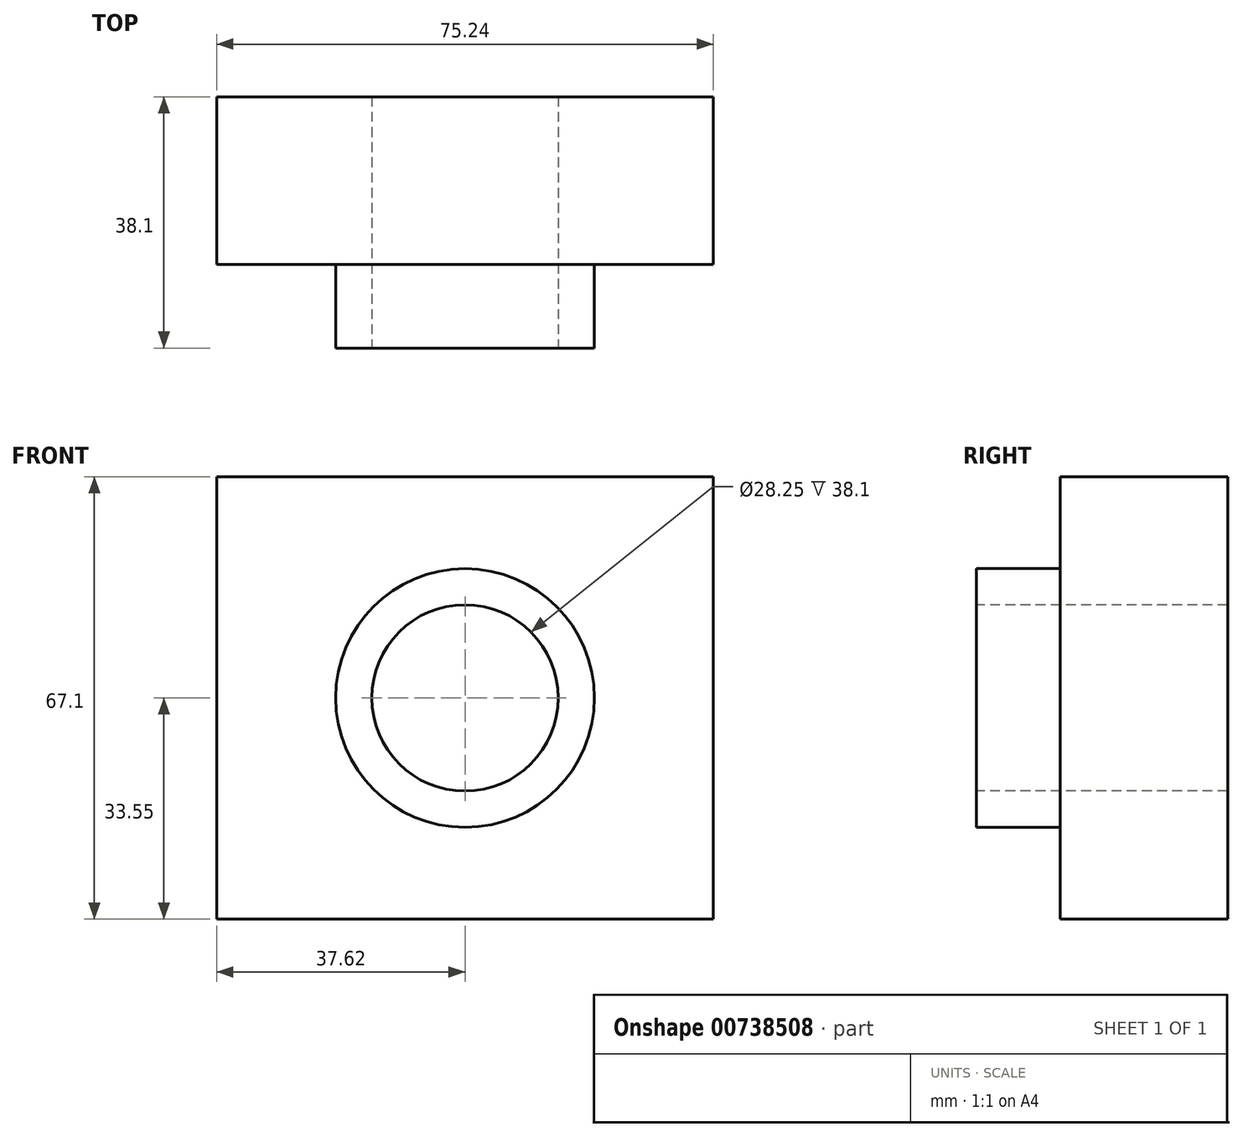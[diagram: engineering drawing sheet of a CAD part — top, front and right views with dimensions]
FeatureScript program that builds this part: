
annotation { "Feature Type Name" : "Feature", "Feature Type Description" : "" }
export const myFeature = defineFeature(function(context is Context, id is Id, definition is map)
    precondition{}
    {
        {
            var Q0;
            Q0=qCreatedBy(makeId("Front.planeOp"),FACE);
            var sketch = newSketch(context, id + "F0", { "sketchPlane" : qUnion([Q0])});
            skLineSegment(sketch, "E0.bottom", {"start": v(37.62, 33.55) * mm, "end": v(-37.62, 33.55) * mm});
            skLineSegment(sketch, "E0.top", {"start": v(37.62, -33.55) * mm, "end": v(-37.62, -33.55) * mm});
            skLineSegment(sketch, "E0.left", {"start": v(37.62, 33.55) * mm, "end": v(37.62, -33.55) * mm});
            skLineSegment(sketch, "E0.right", {"start": v(-37.62, 33.55) * mm, "end": v(-37.62, -33.55) * mm});
            skPoint(sketch, "E0.middle", {"position": v(0, 0) * mm});
            skSolve(sketch);
        }
        {
            var Q0;
            Q0=makeQuery(id+"F0.imprint","IMPRINT",FACE,{"disambiguationData":[TD([[makeQuery(id+"F0.imprint","IMPRINT",EDGE,{"derivedFrom":sQuery(id+"F0.wireOp",EDGE,"E0.bottom")}),1.0]])]});
            extrude(context, id + "F1", {"entities" : qUnion([Q0]), "depth" : 25.4 * mm, "offsetDistance" : 25.4 * mm});
        }
        {
            var Q0;
            Q0=makeQuery(id+"F1.opExtrude","CAP_FACE",FACE,{"disambiguationData":[OSD([sQuery(id+"F0.wireOp",EDGE,"E0.bottom"),sQuery(id+"F0.wireOp",EDGE,"E0.top"),sQuery(id+"F0.wireOp",EDGE,"E0.left"),sQuery(id+"F0.wireOp",EDGE,"E0.right")])],"isStart":false});
            var sketch = newSketch(context, id + "F2", { "sketchPlane" : qUnion([Q0])});
            skCircle(sketch, "E1", {"center": v(0, 0) * mm, "radius": 14.12 * mm});
            skCircle(sketch, "E2", {"center": v(0, 0) * mm, "radius": 19.6 * mm});
            skSolve(sketch);
        }
        {
            var Q0;
            Q0=makeQuery(id+"F2.imprint","IMPRINT",FACE,{"disambiguationData":[TD([[makeQuery(id+"F2.imprint","IMPRINT",EDGE,{"derivedFrom":sQuery(id+"F2.wireOp",EDGE,"E1")}),1.0]])]});
            extrude(context, id + "F3", {"entities" : qUnion([Q0]), "operationType" : NewBodyOperationType.REMOVE, "endBound" : BoundingType.THROUGH_ALL, "oppositeDirection" : true, "depth" : 25.4 * mm, "offsetDistance" : 25.4 * mm});
        }
        {
            var Q0;
            Q0=makeQuery(id+"F2.imprint","IMPRINT",FACE,{"disambiguationData":[TD([[makeQuery(id+"F2.imprint","IMPRINT",EDGE,{"derivedFrom":sQuery(id+"F2.wireOp",EDGE,"E1")}),-1.0]])]});
            extrude(context, id + "F4", {"entities" : qUnion([Q0]), "operationType" : NewBodyOperationType.ADD, "depth" : 12.7 * mm, "offsetDistance" : 25.4 * mm});
        }
    });
